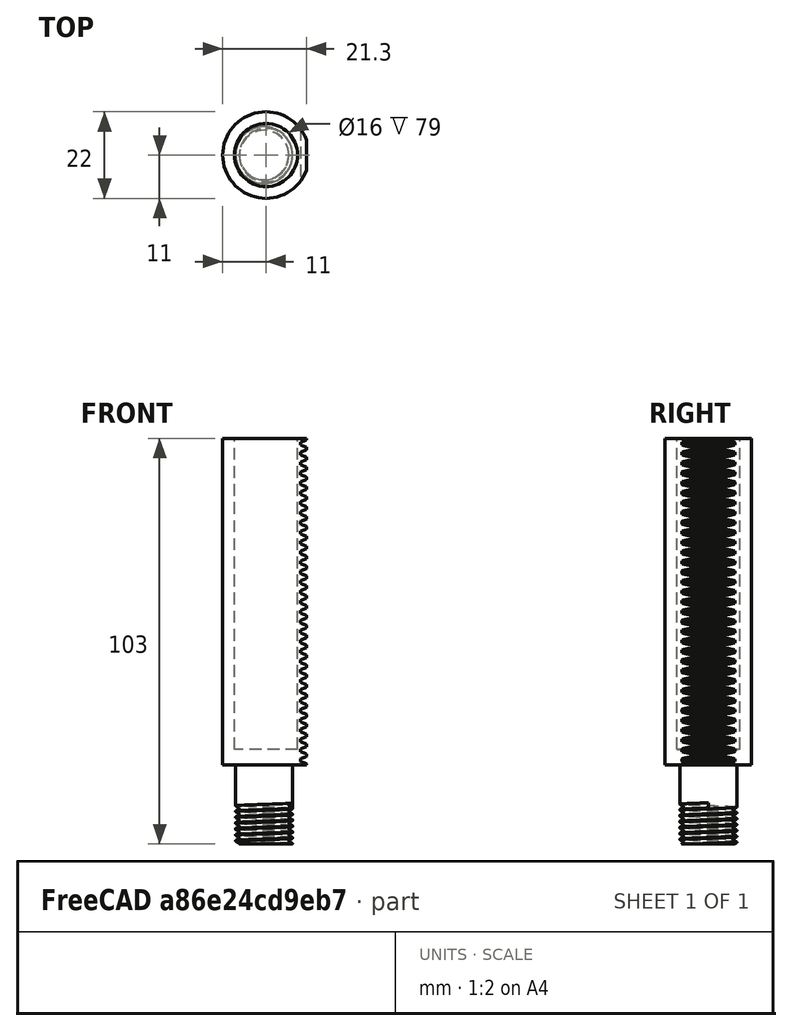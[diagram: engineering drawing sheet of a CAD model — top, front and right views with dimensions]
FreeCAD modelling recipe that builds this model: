
FCSTD DOCUMENT  (FreeCAD 0.18R16110 (Git))
Label: Gear_Rack
License: All rights reserved
LicenseURL: http://en.wikipedia.org/wiki/All_rights_reserved
objects: Part::Cylinder×3, Spreadsheet::Sheet×2, Part::Cut×2, Part::FeaturePython×1, Sketcher::SketchObject×1, Part::MultiCommon×1, Part::Helix×1, Part::Sweep×1, Part::MultiFuse×1, Mesh::Feature×1
note: 11 computed .brp shape members not serialized (recipe doc carries the construction recipe); baked Part::Feature solids carry a one-line shape summary decoded from their .brp

FEATURE [Part::FeaturePython] InvoluteRack  # WARN: FeaturePython — macro-defined, semantics opaque (R4)
  Placement = pos=(0,0,0) rot=(1,0,0;1.5708rad)
  beta = 0
  double_helix = false
  head = 0
  height = 24
  module = 0.8
  pressure_angle = 20
  teeth = 36
  thickness = 20
FEATURE [Sketcher::SketchObject] CopySketch017  label="sketch_bolt001"
  Placement = pos=(0,0,0) rot=(1,0,0;1.5708rad)
  expr: Constraints[9] = Spreadsheet006.winkel
  expr: Constraints[17] = Spreadsheet006.pitch / 2
  expr: Constraints[26] = Spreadsheet006.threaddepth_tol * (1 - 1 / 4 - 1 / 8) - sqrt(1 / 6 ^ 2 - (tan(Spreadsheet006.winkel / 2) / 4) ^ 2) * Spreadsheet006.threaddepth_tol
  expr: Constraints[7] = Spreadsheet006.threaddepth_tol * (1 - 1 / 8) * tan(Spreadsheet006.winkel / 2)
  expr: Constraints[1] = Spreadsheet006.bolt_ra + 0.001
  expr: Constraints[11] = Spreadsheet006.winkel
  expr: Constraints[20] = Spreadsheet006.threaddepth_tol * (1 - 1 / 4 - 1 / 8)
  sketch-geometry (9):
    g0: LineSegment [constr] StartX=0 StartY=0 StartZ=0 EndX=7.23766 EndY=0 EndZ=0
    g1: LineSegment StartX=7.23766 StartY=-0.09375 StartZ=0 EndX=7.23766 EndY=-0.75 EndZ=0
    g2: LineSegment StartX=7.23766 StartY=-0.75 StartZ=0 EndX=7.23766 EndY=-1.40625 EndZ=0
    g3: LineSegment StartX=7.23766 StartY=-0.09375 StartZ=0 EndX=6.42576 EndY=-0.5625 EndZ=0
    g4: LineSegment StartX=7.23766 StartY=-1.40625 StartZ=0 EndX=6.42576 EndY=-0.9375 EndZ=0
    g5: LineSegment [constr] StartX=6.42576 StartY=-0.5625 StartZ=0 EndX=6.42576 EndY=-0.9375 EndZ=0
    g6: LineSegment [constr] StartX=7.23766 StartY=-0.75 StartZ=0 EndX=7.23766 EndY=0 EndZ=0
    g7: LineSegment [constr] StartX=7.23766 StartY=-0.75 StartZ=0 EndX=6.53401 EndY=-0.75 EndZ=0
    g8: ArcOfCircle CenterX=6.53401 CenterY=-0.75 CenterZ=0 NormalX=0 NormalY=0 NormalZ=1 AngleXU=0 Radius=0.216506 StartAngle=2.0944 EndAngle=4.18879
  constraints (27):
    c: Horizontal(g0)
    c: DistanceX(g0,g0) = 7.23766
    c: Coincident(g-1,g0)
    c: Vertical(g1)
    c: Coincident(g2,g1)
    c: Vertical(g2)
    c: Equal(g1,g2)
    c: DistanceY(g1,g1) = 0.65625
    c: Coincident(g3,g1)
    c: Angle(g3,g1) = 1.0472
    c: Coincident(g4,g2)
    c: Angle(g2,g4) = 1.0472
    c: Vertical(g5)
    c: Coincident(g4,g5)
    c: Equal(g4,g3)
    c: Coincident(g6,g1)
    c: Vertical(g6)
    c: DistanceY(g6,g6) = 0.75
    c: Coincident(g6,g0)
    c: Coincident(g3,g5)
    c: DistanceX(g4,g4) = 0.811899
    c: Coincident(g7,g1)
    c: Horizontal(g7)
    c: Coincident(g8,g7)
    c: Coincident(g8,g3)
    c: Coincident(g8,g4)
    c: DistanceX(g7,g7) = 0.703646
FEATURE [Spreadsheet::Sheet] Spreadsheet
  cells = A1=steigung; B1=h; D1(pitch)=1; F1=bauhöhe; G1(height)=11; A2=Gewindetiefe; B2=t; C2=h*cos(30°); D2(threaddepth)==pitch * cos(30); F2=helix height; G2(height_h)=19; C3=threaddepth tol; D3(threaddepth_tol)==(pitch + tolerance_fla * cos(30)) * cos(30); F3=Flanken - Tolerance; G3(tolerance_fla)=0; A4=Nut; F4=Radien - Tolerance; G4(tolerance)=0.2; A5=ra; E5(nut_ra)==(bolt_ri + bolt_si + threaddepth + nut_sa) * 0 + 7.7; A6=sa; E6(nut_sa)=1; A7=ri; E7(nut_ri)==(nb_centerline - threaddepth / 2 + threaddepth / 4 + tolerance) * 1 + 8 * 0; A9=Bolt; A10=ri; E10(bolt_ri)==(spring_sh + spring_sj * 0 + spring_rh) * 0 + 8 - bolt_si - threaddepth / 4 - tolerance; A11=si; E11(bolt_si)=2; G11==sqrt(1 / 6 ^ 2 - (tan(30) / 4) ^ 2) * Spreadsheet.threaddepth_tol; A12=ra; E12(bolt_ra)==nb_centerline + threaddepth / 2 - threaddepth / 8 - tolerance; A14=Nut/Bold centerline; E14(nb_centerline)==bolt_ri + bolt_si + threaddepth / 2; F14==8 - 2 - threaddepth / 8 - tolerance; A16=Spring rh; E16(spring_rh)=4.69175; A17=hülsenstärke sh; E17(spring_sh)=1; A18=join rest   js; E18(spring_sj)=1.4; A21=join heigtht jh; B21(spring_jh)=3; A22=join ri; B22(spring_jri)==spring_rh + spring_sh + tolerance_fla
FEATURE [Spreadsheet::Sheet] Spreadsheet006
  cells = A1=steigung; B1=h; D1(pitch)=1.5; F1=bauhöhe; G1(height)=8; A2=Gewindetiefe; B2=t; C2=h*cos(30°); D2(threaddepth)==pitch * cos(winkel / 2); F2=helix height; G2(height_h)=19; A3=Winkel; B3(winkel)==60°; C3=threaddepth tol; D3(threaddepth_tol)==(pitch + tolerance_fla * cos(winkel / 2)) * cos(winkel / 2); F3=Flanken - Tolerance; G3(tolerance_fla)=0; A4=Nut; F4=Radien - Tolerance; G4(tolerance)=0.2; A5=ra; E5(nut_ra)==bolt_ri + bolt_si + threaddepth + nut_sa; A6=sa; E6(nut_sa)=1.2; A7=ri; E7(nut_ri)==nb_centerline - threaddepth / 2 + threaddepth / 4 + tolerance; F7==E7 * 2; A9=Bolt; A10=ri; E10(bolt_ri)=5.1; F10==15.8 / 2; A11=si; E11(bolt_si)=1.2; G11==sqrt(1 / 6 ^ 2 - (tan(30) / 4) ^ 2) * Spreadsheet.threaddepth_tol; A12=ra; E12(bolt_ra)==nb_centerline + threaddepth / 2 - threaddepth / 8 - tolerance; F12==13.2 / 2; A14=Nut/Bold centerline; E14(nb_centerline)==bolt_ri + bolt_si + threaddepth / 2; F14==18.3 / 2; A16=Spring rh; E16(spring_rh)=1.8; A17=hülsenstärke sh; E17(spring_sh)=1; A18=join rest   js; E18(spring_sj)=1.4; A21=join heigtht jh; B21(spring_jh)=3; A22=join ri; B22(spring_jri)==spring_rh + spring_sh + tolerance_fla
FEATURE [Part::Cylinder] Cylinder102  label="Zylinder102"
  Angle = 360
  AttacherType = Attacher::AttachEngine3D
  Height = 83
  Placement = pos=(-9.5,-12,0) rot=(0,0,1;0rad)
  Radius = 11
FEATURE [Part::MultiCommon] Common
  Shapes = -> [Cylinder102,InvoluteRack]
FEATURE [Part::Cylinder] Cylinder103  label="Zylinder103"
  Angle = 360
  AttacherType = Attacher::AttachEngine3D
  Height = 95
  Placement = pos=(-9.5,-12,4) rot=(0,0,1;0rad)
  Radius = 8
FEATURE [Part::Cut] Cut
  Base = -> Common
  Tool = -> Cylinder103
FEATURE [Part::Cylinder] Cylinder184  label="Zylinder184"
  Angle = 360
  AttacherType = Attacher::AttachEngine3D
  Height = 20
  Radius = 7.23666
  expr: Radius = Spreadsheet006.bolt_ra
FEATURE [Part::Helix] Helix017  label="Helix_bolt001"
  Angle = 0
  AttacherType = Attacher::AttachEngine3D
  Height = 19
  LocalCoord = 0
  Pitch = 1.5
  Radius = 7.23666
  Style = 1
  expr: Height = Spreadsheet006.height_h
  expr: Pitch = Spreadsheet006.pitch
  expr: Radius = Spreadsheet006.bolt_ra
FEATURE [Part::Sweep] Sweep011
  Frenet = true
  Sections = -> [CopySketch017]
  Solid = true
  Spine = -> Helix017 [Edge1,Edge2,Edge3,Edge4,Edge5,Edge6,Edge7]
  Transition = 1
FEATURE [Part::Cut] Cut013
  Base = -> Cylinder184
  Placement = pos=(-10,-12,-20) rot=(0,0,1;0rad)
  Tool = -> Sweep011
FEATURE [Part::MultiFuse] Fusion  label="Gear_Rack"
  Shapes = -> [Cut,Cut013]
FEATURE [Mesh::Feature] Mesh013  label="Gear_rack(Meshed)"
  Placement = pos=(0,0,0) rot=(1,0,0;0.017453rad)
